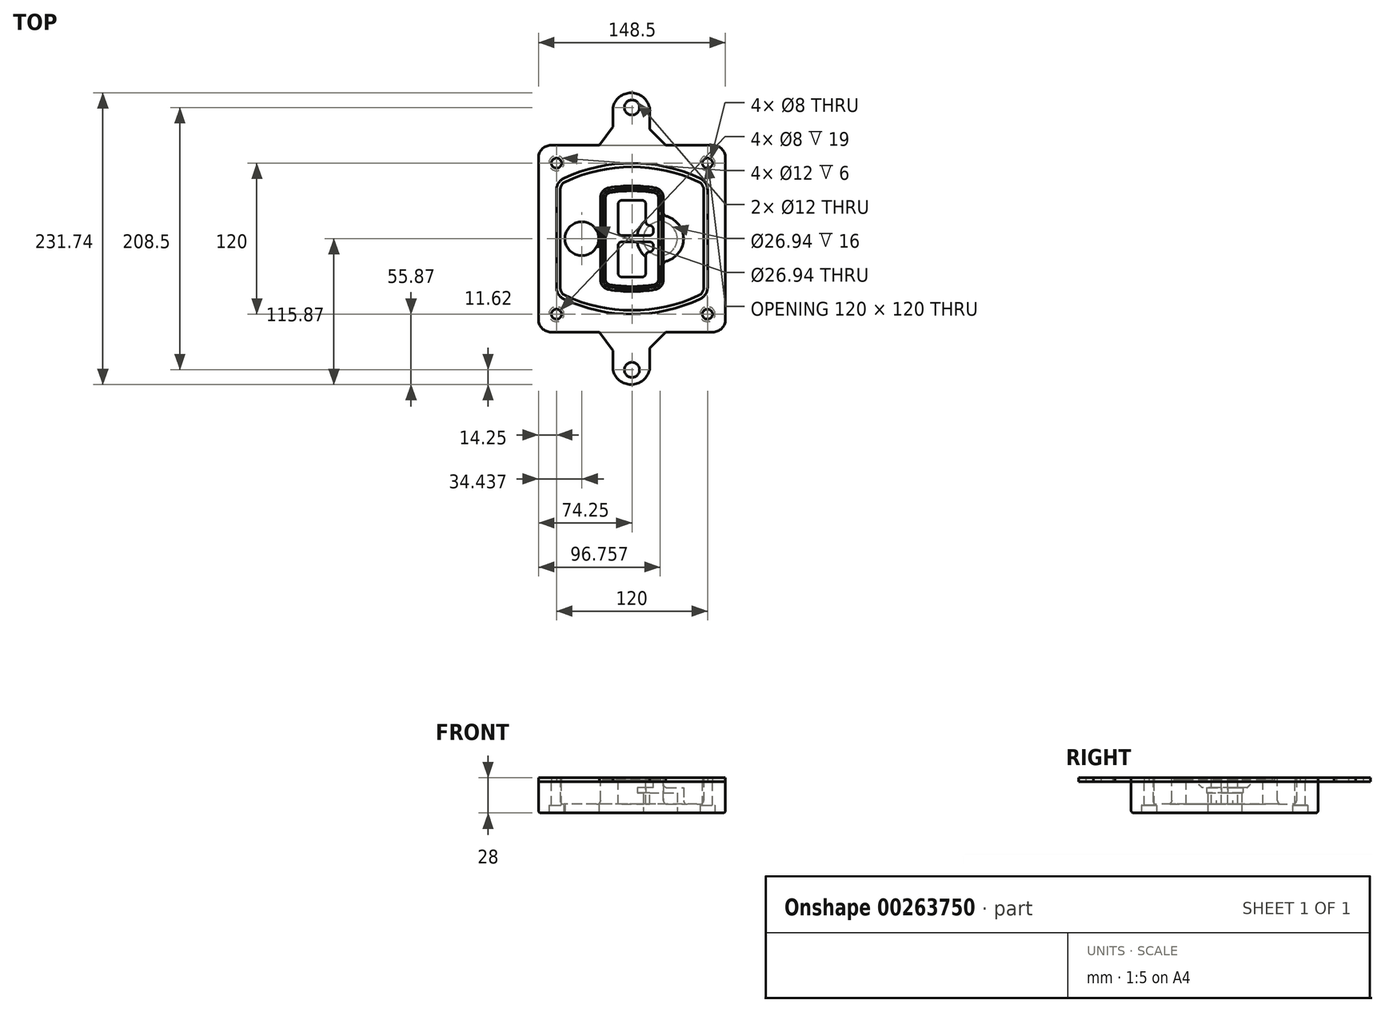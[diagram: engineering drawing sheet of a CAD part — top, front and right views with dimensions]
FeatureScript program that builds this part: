
annotation { "Feature Type Name" : "Feature", "Feature Type Description" : "" }
export const myFeature = defineFeature(function(context is Context, id is Id, definition is map)
    precondition{}
    {
        {
            var Q0;
            Q0=qCreatedBy(makeId("Top.planeOp"),FACE);
            var sketch = newSketch(context, id + "F0", { "sketchPlane" : qUnion([Q0])});
            skPoint(sketch, "E0.rect.middle", {"position": v(0, 0) * mm});
            skLineSegment(sketch, "E1.bottom", {"start": v(-64.25, -74.25) * mm, "end": v(64.25, -74.25) * mm});
            skLineSegment(sketch, "E1.top", {"start": v(-64.25, 74.25) * mm, "end": v(64.25, 74.25) * mm});
            skLineSegment(sketch, "E1.left", {"start": v(-74.25, -64.25) * mm, "end": v(-74.25, 64.25) * mm});
            skLineSegment(sketch, "E1.right", {"start": v(74.25, -64.25) * mm, "end": v(74.25, 64.25) * mm});
            skLineSegment(sketch, "E2", {"start": v(-74.25, 74.25) * mm, "end": v(74.25, -74.25) * mm, "construction": true});
            skLineSegment(sketch, "E3", {"start": v(74.25, 74.25) * mm, "end": v(-74.25, -74.25) * mm, "construction": true});
            skCircle(sketch, "E4", {"center": v(-60, 60) * mm, "radius": 4 * mm});
            skCircle(sketch, "E5", {"center": v(60, 60) * mm, "radius": 4 * mm});
            skCircle(sketch, "E6", {"center": v(60, -60) * mm, "radius": 4 * mm});
            skCircle(sketch, "E7", {"center": v(-60, -60) * mm, "radius": 4 * mm});
            skLineSegment(sketch, "E8", {"start": v(-60, 60) * mm, "end": v(60, 60) * mm, "construction": true});
            skLineSegment(sketch, "E9", {"start": v(60, 60) * mm, "end": v(60, -60) * mm, "construction": true});
            skLineSegment(sketch, "E10", {"start": v(60, -60) * mm, "end": v(-60, -60) * mm, "construction": true});
            skLineSegment(sketch, "E11", {"start": v(-60, -60) * mm, "end": v(-60, 60) * mm, "construction": true});
            skLineSegment(sketch, "E12", {"start": v(-60, 38.83) * mm, "end": v(-60, -38.83) * mm});
            skLineSegment(sketch, "E13", {"start": v(60, 38.83) * mm, "end": v(60, -38.83) * mm});
            skArc(sketch, "E14", {"start": v(54.26, 47.88) * mm, "mid": v(0, 60) * mm, "end": v(-54.26, 47.88) * mm});
            skArc(sketch, "E15", {"start": v(-54.26, -47.88) * mm, "mid": v(0, -60) * mm, "end": v(54.26, -47.88) * mm});
            skLineSegment(sketch, "E16", {"start": v(-60, 0) * mm, "end": v(60, 0) * mm, "construction": true});
            skPoint(sketch, "E17.visualSharp", {"position": v(-60, -45) * mm});
            skArc(sketch, "E17.filletArc", {"start": v(-60, -38.83) * mm, "mid": v(-58.44, -44.2) * mm, "end": v(-54.26, -47.88) * mm});
            skPoint(sketch, "E18.visualSharp", {"position": v(-60, 45) * mm});
            skArc(sketch, "E18.filletArc", {"start": v(-54.26, 47.88) * mm, "mid": v(-58.44, 44.2) * mm, "end": v(-60, 38.83) * mm});
            skPoint(sketch, "E19.visualSharp", {"position": v(60, 45) * mm});
            skArc(sketch, "E19.filletArc", {"start": v(60, 38.83) * mm, "mid": v(58.44, 44.2) * mm, "end": v(54.26, 47.88) * mm});
            skPoint(sketch, "E20.visualSharp", {"position": v(60, -45) * mm});
            skArc(sketch, "E20.filletArc", {"start": v(54.26, -47.88) * mm, "mid": v(58.44, -44.2) * mm, "end": v(60, -38.83) * mm});
            skPoint(sketch, "E21.visualSharp", {"position": v(-74.25, 74.25) * mm});
            skArc(sketch, "E21.filletArc", {"start": v(-64.25, 74.25) * mm, "mid": v(-71.32, 71.32) * mm, "end": v(-74.25, 64.25) * mm});
            skPoint(sketch, "E22.visualSharp", {"position": v(74.25, 74.25) * mm});
            skArc(sketch, "E22.filletArc", {"start": v(74.25, 64.25) * mm, "mid": v(71.32, 71.32) * mm, "end": v(64.25, 74.25) * mm});
            skPoint(sketch, "E23.visualSharp", {"position": v(74.25, -74.25) * mm});
            skArc(sketch, "E23.filletArc", {"start": v(64.25, -74.25) * mm, "mid": v(71.32, -71.32) * mm, "end": v(74.25, -64.25) * mm});
            skPoint(sketch, "E24.visualSharp", {"position": v(-74.25, -74.25) * mm});
            skArc(sketch, "E24.filletArc", {"start": v(-74.25, -64.25) * mm, "mid": v(-71.32, -71.32) * mm, "end": v(-64.25, -74.25) * mm});
            skArc(sketch, "E25.0", {"start": v(57, 38.83) * mm, "mid": v(55.9, 42.58) * mm, "end": v(52.98, 45.17) * mm});
            skLineSegment(sketch, "E25.1", {"start": v(57, 38.83) * mm, "end": v(57, -38.83) * mm});
            skArc(sketch, "E25.2", {"start": v(52.98, -45.17) * mm, "mid": v(55.9, -42.58) * mm, "end": v(57, -38.83) * mm});
            skArc(sketch, "E25.3", {"start": v(-52.98, -45.17) * mm, "mid": v(0, -57) * mm, "end": v(52.98, -45.17) * mm});
            skArc(sketch, "E25.4", {"start": v(-57, -38.83) * mm, "mid": v(-55.9, -42.58) * mm, "end": v(-52.98, -45.17) * mm});
            skArc(sketch, "E25.5", {"start": v(52.98, 45.17) * mm, "mid": v(0, 57) * mm, "end": v(-52.98, 45.17) * mm});
            skLineSegment(sketch, "E25.6", {"start": v(-57, 38.83) * mm, "end": v(-57, -38.83) * mm});
            skArc(sketch, "E25.7", {"start": v(-52.98, 45.17) * mm, "mid": v(-55.9, 42.58) * mm, "end": v(-57, 38.83) * mm});
            skArc(sketch, "E26.0", {"start": v(-55.96, 51.5) * mm, "mid": v(-61.82, 46.33) * mm, "end": v(-64, 38.83) * mm});
            skArc(sketch, "E26.1", {"start": v(55.96, 51.5) * mm, "mid": v(0, 64) * mm, "end": v(-55.96, 51.5) * mm});
            skArc(sketch, "E26.2", {"start": v(64, 38.83) * mm, "mid": v(61.82, 46.33) * mm, "end": v(55.96, 51.5) * mm});
            skLineSegment(sketch, "E26.3", {"start": v(64, 38.83) * mm, "end": v(64, -38.83) * mm});
            skArc(sketch, "E26.4", {"start": v(55.96, -51.5) * mm, "mid": v(61.82, -46.33) * mm, "end": v(64, -38.83) * mm});
            skLineSegment(sketch, "E26.5", {"start": v(-64, 38.83) * mm, "end": v(-64, -38.83) * mm});
            skArc(sketch, "E26.6", {"start": v(-55.96, -51.5) * mm, "mid": v(0, -64) * mm, "end": v(55.96, -51.5) * mm});
            skArc(sketch, "E26.7", {"start": v(-64, -38.83) * mm, "mid": v(-61.82, -46.33) * mm, "end": v(-55.96, -51.5) * mm});
            skSolve(sketch);
        }
        {
            var Q0;
            Q0=makeQuery(id+"F0.imprint","IMPRINT",FACE,{"disambiguationData":[TD([[makeQuery(id+"F0.imprint","IMPRINT",EDGE,{"derivedFrom":sQuery(id+"F0.wireOp",EDGE,"E1.bottom")}),1.0]])]});
            var Q1;
            Q1=makeQuery(id+"F0.imprint","IMPRINT",FACE,{"disambiguationData":[TD([[makeQuery(id+"F0.imprint","IMPRINT",EDGE,{"derivedFrom":sQuery(id+"F0.wireOp",EDGE,"E12")}),1.0]])]});
            var Q2;
            Q2=makeQuery(id+"F0.imprint","IMPRINT",FACE,{"disambiguationData":[TD([[makeQuery(id+"F0.imprint","IMPRINT",EDGE,{"derivedFrom":sQuery(id+"F0.wireOp",EDGE,"E25.0")}),1.0]])]});
            var Q3;
            Q3=makeQuery(id+"F0.imprint","IMPRINT",FACE,{"disambiguationData":[TD([[makeQuery(id+"F0.imprint","IMPRINT",EDGE,{"derivedFrom":sQuery(id+"F0.wireOp",EDGE,"E12")}),-1.0]])]});
            extrude(context, id + "F1", {"entities" : qUnion([Q0, Q1, Q2, Q3]), "oppositeDirection" : true, "depth" : 25 * mm});
        }
        {
            var Q0;
            Q0=makeQuery(id+"F0.imprint","IMPRINT",FACE,{"disambiguationData":[TD([[makeQuery(id+"F0.imprint","IMPRINT",EDGE,{"derivedFrom":sQuery(id+"F0.wireOp",EDGE,"E12")}),1.0]])]});
            extrude(context, id + "F2", {"entities" : qUnion([Q0]), "operationType" : NewBodyOperationType.ADD, "depth" : 3 * mm});
        }
        {
            var Q0;
            Q0=makeQuery(id+"F0.imprint","IMPRINT",FACE,{"disambiguationData":[TD([[makeQuery(id+"F0.imprint","IMPRINT",EDGE,{"derivedFrom":sQuery(id+"F0.wireOp",EDGE,"E25.0")}),1.0]])]});
            extrude(context, id + "F3", {"entities" : qUnion([Q0]), "operationType" : NewBodyOperationType.REMOVE, "oppositeDirection" : true, "depth" : 18 * mm});
        }
        {
            var Q0;
            Q0=makeQuery(id+"F2.opExtrude","CAP_FACE",FACE,{"disambiguationData":[OSD([sQuery(id+"F0.wireOp",EDGE,"E12"),sQuery(id+"F0.wireOp",EDGE,"E13"),sQuery(id+"F0.wireOp",EDGE,"E14"),sQuery(id+"F0.wireOp",EDGE,"E15"),sQuery(id+"F0.wireOp",EDGE,"E17.filletArc"),sQuery(id+"F0.wireOp",EDGE,"E18.filletArc"),sQuery(id+"F0.wireOp",EDGE,"E19.filletArc"),sQuery(id+"F0.wireOp",EDGE,"E20.filletArc"),sQuery(id+"F0.wireOp",EDGE,"E25.0"),sQuery(id+"F0.wireOp",EDGE,"E25.1"),sQuery(id+"F0.wireOp",EDGE,"E25.2"),sQuery(id+"F0.wireOp",EDGE,"E25.3"),sQuery(id+"F0.wireOp",EDGE,"E25.4"),sQuery(id+"F0.wireOp",EDGE,"E25.5"),sQuery(id+"F0.wireOp",EDGE,"E25.6"),sQuery(id+"F0.wireOp",EDGE,"E25.7")])],"isStart":false});
            var sketch = newSketch(context, id + "F4", { "sketchPlane" : qUnion([Q0])});
            skArc(sketch, "E27.0", {"start": v(-18.34, -40.45) * mm, "mid": v(0, -42) * mm, "end": v(18.34, -40.45) * mm});
            skArc(sketch, "E28.0", {"start": v(18.34, 40.45) * mm, "mid": v(0, 42) * mm, "end": v(-18.34, 40.45) * mm});
            skLineSegment(sketch, "E29", {"start": v(-25, 32.57) * mm, "end": v(-25, -32.57) * mm});
            skLineSegment(sketch, "E30", {"start": v(25, 32.57) * mm, "end": v(25, -32.57) * mm});
            skLineSegment(sketch, "E31", {"start": v(-25, 39.1) * mm, "end": v(25, 39.1) * mm, "construction": true});
            skLineSegment(sketch, "E32", {"start": v(-25, -39.1) * mm, "end": v(25, -39.1) * mm, "construction": true});
            skPoint(sketch, "E33.visualSharp", {"position": v(-25, 39.1) * mm});
            skArc(sketch, "E33.filletArc", {"start": v(-18.34, 40.45) * mm, "mid": v(-23.11, 37.73) * mm, "end": v(-25, 32.57) * mm});
            skPoint(sketch, "E34.visualSharp", {"position": v(25, 39.1) * mm});
            skArc(sketch, "E34.filletArc", {"start": v(25, 32.57) * mm, "mid": v(23.11, 37.73) * mm, "end": v(18.34, 40.45) * mm});
            skPoint(sketch, "E35.visualSharp", {"position": v(25, -39.1) * mm});
            skArc(sketch, "E35.filletArc", {"start": v(18.34, -40.45) * mm, "mid": v(23.11, -37.73) * mm, "end": v(25, -32.57) * mm});
            skPoint(sketch, "E36.visualSharp", {"position": v(-25, -39.1) * mm});
            skArc(sketch, "E36.filletArc", {"start": v(-25, -32.57) * mm, "mid": v(-23.11, -37.73) * mm, "end": v(-18.34, -40.45) * mm});
            skArc(sketch, "E37.0", {"start": v(52.98, 45.17) * mm, "mid": v(0, 57) * mm, "end": v(-52.98, 45.17) * mm});
            skArc(sketch, "E37.1", {"start": v(-52.98, 45.17) * mm, "mid": v(-55.9, 42.58) * mm, "end": v(-57, 38.83) * mm});
            skLineSegment(sketch, "E37.2", {"start": v(-57, 38.83) * mm, "end": v(-57, -38.83) * mm});
            skArc(sketch, "E37.3", {"start": v(-57, -38.83) * mm, "mid": v(-55.9, -42.58) * mm, "end": v(-52.98, -45.17) * mm});
            skArc(sketch, "E37.4", {"start": v(-52.98, -45.17) * mm, "mid": v(0, -57) * mm, "end": v(52.98, -45.17) * mm});
            skArc(sketch, "E37.5", {"start": v(52.98, -45.17) * mm, "mid": v(55.9, -42.58) * mm, "end": v(57, -38.83) * mm});
            skLineSegment(sketch, "E37.6", {"start": v(57, 38.83) * mm, "end": v(57, -38.83) * mm});
            skArc(sketch, "E37.7", {"start": v(57, 38.83) * mm, "mid": v(55.9, 42.58) * mm, "end": v(52.98, 45.17) * mm});
            skLineSegment(sketch, "E38.0", {"start": v(23, 32.57) * mm, "end": v(23, -32.57) * mm});
            skArc(sketch, "E38.1", {"start": v(18, -38.48) * mm, "mid": v(21.58, -36.44) * mm, "end": v(23, -32.57) * mm});
            skArc(sketch, "E38.2", {"start": v(-18, -38.48) * mm, "mid": v(0, -40) * mm, "end": v(18, -38.48) * mm});
            skArc(sketch, "E38.3", {"start": v(-23, -32.57) * mm, "mid": v(-21.58, -36.44) * mm, "end": v(-18, -38.48) * mm});
            skLineSegment(sketch, "E38.4", {"start": v(-23, 32.57) * mm, "end": v(-23, -32.57) * mm});
            skArc(sketch, "E38.5", {"start": v(23, 32.57) * mm, "mid": v(21.58, 36.44) * mm, "end": v(18, 38.48) * mm});
            skArc(sketch, "E38.6", {"start": v(-18, 38.48) * mm, "mid": v(-21.58, 36.44) * mm, "end": v(-23, 32.57) * mm});
            skArc(sketch, "E38.7", {"start": v(18, 38.48) * mm, "mid": v(0, 40) * mm, "end": v(-18, 38.48) * mm});
            skArc(sketch, "E39.0", {"start": v(21, 32.57) * mm, "mid": v(20.06, 35.15) * mm, "end": v(17.67, 36.5) * mm});
            skLineSegment(sketch, "E39.1", {"start": v(21, 32.57) * mm, "end": v(21, -32.57) * mm});
            skArc(sketch, "E39.2", {"start": v(17.67, -36.5) * mm, "mid": v(20.06, -35.15) * mm, "end": v(21, -32.57) * mm});
            skArc(sketch, "E39.3", {"start": v(-17.67, -36.5) * mm, "mid": v(0, -38) * mm, "end": v(17.67, -36.5) * mm});
            skArc(sketch, "E39.4", {"start": v(-21, -32.57) * mm, "mid": v(-20.06, -35.15) * mm, "end": v(-17.67, -36.5) * mm});
            skArc(sketch, "E39.5", {"start": v(17.67, 36.5) * mm, "mid": v(0, 38) * mm, "end": v(-17.67, 36.5) * mm});
            skLineSegment(sketch, "E39.6", {"start": v(-21, 32.57) * mm, "end": v(-21, -32.57) * mm});
            skArc(sketch, "E39.7", {"start": v(-17.67, 36.5) * mm, "mid": v(-20.06, 35.15) * mm, "end": v(-21, 32.57) * mm});
            skLineSegment(sketch, "E40", {"start": v(-25, 0) * mm, "end": v(25, 0) * mm, "construction": true});
            skLineSegment(sketch, "E41", {"start": v(-11, 5.5) * mm, "end": v(-11, 27.5) * mm});
            skLineSegment(sketch, "E42", {"start": v(-8, 30.5) * mm, "end": v(8, 30.5) * mm});
            skLineSegment(sketch, "E43", {"start": v(11, 27.5) * mm, "end": v(11, 13.5) * mm});
            skLineSegment(sketch, "E44", {"start": v(14, 10.5) * mm, "end": v(14, 10.5) * mm});
            skLineSegment(sketch, "E45", {"start": v(17, 7.5) * mm, "end": v(17, 5.5) * mm});
            skLineSegment(sketch, "E46", {"start": v(14, 2.5) * mm, "end": v(-8, 2.5) * mm});
            skPoint(sketch, "E47.visualSharp", {"position": v(-11, 30.5) * mm});
            skArc(sketch, "E47.filletArc", {"start": v(-8, 30.5) * mm, "mid": v(-10.12, 29.62) * mm, "end": v(-11, 27.5) * mm});
            skPoint(sketch, "E48.visualSharp", {"position": v(11, 30.5) * mm});
            skArc(sketch, "E48.filletArc", {"start": v(11, 27.5) * mm, "mid": v(10.12, 29.62) * mm, "end": v(8, 30.5) * mm});
            skPoint(sketch, "E49.visualSharp", {"position": v(11, 10.5) * mm});
            skArc(sketch, "E49.filletArc", {"start": v(11, 13.5) * mm, "mid": v(11.88, 11.38) * mm, "end": v(14, 10.5) * mm});
            skPoint(sketch, "E50.visualSharp", {"position": v(17, 10.5) * mm});
            skArc(sketch, "E50.filletArc", {"start": v(17, 7.5) * mm, "mid": v(16.12, 9.62) * mm, "end": v(14, 10.5) * mm});
            skPoint(sketch, "E51.visualSharp", {"position": v(17, 2.5) * mm});
            skArc(sketch, "E51.filletArc", {"start": v(14, 2.5) * mm, "mid": v(16.12, 3.38) * mm, "end": v(17, 5.5) * mm});
            skPoint(sketch, "E52.visualSharp", {"position": v(-11, 2.5) * mm});
            skArc(sketch, "E52.filletArc", {"start": v(-11, 5.5) * mm, "mid": v(-10.12, 3.38) * mm, "end": v(-8, 2.5) * mm});
            skLineSegment(sketch, "E53.0.MirrorCS", {"start": v(14, -2.5) * mm, "end": v(-8, -2.5) * mm});
            skArc(sketch, "E54.0.MirrorCS", {"start": v(-11, -5.5) * mm, "mid": v(-10.12, -3.38) * mm, "end": v(-8, -2.5) * mm});
            skLineSegment(sketch, "E55.0.MirrorCS", {"start": v(-11, -5.5) * mm, "end": v(-11, -27.5) * mm});
            skArc(sketch, "E56.0.MirrorCS", {"start": v(-8, -30.5) * mm, "mid": v(-10.12, -29.62) * mm, "end": v(-11, -27.5) * mm});
            skLineSegment(sketch, "E57.0.MirrorCS", {"start": v(-8, -30.5) * mm, "end": v(8, -30.5) * mm});
            skArc(sketch, "E58.0.MirrorCS", {"start": v(11, -27.5) * mm, "mid": v(10.12, -29.62) * mm, "end": v(8, -30.5) * mm});
            skLineSegment(sketch, "E59.0.MirrorCS", {"start": v(11, -27.5) * mm, "end": v(11, -13.5) * mm});
            skArc(sketch, "E60.0.MirrorCS", {"start": v(11, -13.5) * mm, "mid": v(11.88, -11.38) * mm, "end": v(14, -10.5) * mm});
            skArc(sketch, "E61.0.MirrorCS", {"start": v(17, -7.5) * mm, "mid": v(16.12, -9.62) * mm, "end": v(14, -10.5) * mm});
            skLineSegment(sketch, "E62.0.MirrorCS", {"start": v(17, -7.5) * mm, "end": v(17, -5.5) * mm});
            skArc(sketch, "E63.0.MirrorCS", {"start": v(14, -2.5) * mm, "mid": v(16.12, -3.38) * mm, "end": v(17, -5.5) * mm});
            skSolve(sketch);
        }
        {
            var Q0;
            Q0=makeQuery(id+"F4.imprint","IMPRINT",FACE,{"disambiguationData":[TD([[makeQuery(id+"F4.imprint","IMPRINT",EDGE,{"derivedFrom":sQuery(id+"F4.wireOp",EDGE,"E27.0")}),1.0]])]});
            var Q1;
            Q1=makeQuery(id+"F4.imprint","IMPRINT",FACE,{"disambiguationData":[TD([[makeQuery(id+"F4.imprint","IMPRINT",EDGE,{"derivedFrom":sQuery(id+"F4.wireOp",EDGE,"E38.0")}),-1.0]])]});
            var Q2;
            Q2=makeQuery(id+"F4.imprint","IMPRINT",FACE,{"disambiguationData":[TD([[makeQuery(id+"F4.imprint","IMPRINT",EDGE,{"derivedFrom":sQuery(id+"F4.wireOp",EDGE,"E39.0")}),1.0]])]});
            extrude(context, id + "F5", {"entities" : qUnion([Q0, Q1, Q2]), "operationType" : NewBodyOperationType.ADD, "endBound" : BoundingType.UP_TO_NEXT, "oppositeDirection" : true, "depth" : 25 * mm});
        }
        {
            var Q0;
            Q0=makeQuery(id+"F4.imprint","IMPRINT",FACE,{"disambiguationData":[TD([[makeQuery(id+"F4.imprint","IMPRINT",EDGE,{"derivedFrom":sQuery(id+"F4.wireOp",EDGE,"E38.0")}),-1.0]])]});
            extrude(context, id + "F6", {"entities" : qUnion([Q0]), "operationType" : NewBodyOperationType.REMOVE, "oppositeDirection" : true, "depth" : 2 * mm});
        }
        {
            var Q0;
            Q0=makeQuery(id+"F1.opExtrude","CAP_FACE",FACE,{"disambiguationData":[OSD([sQuery(id+"F0.wireOp",EDGE,"E1.bottom"),sQuery(id+"F0.wireOp",EDGE,"E1.top"),sQuery(id+"F0.wireOp",EDGE,"E1.left"),sQuery(id+"F0.wireOp",EDGE,"E1.right"),sQuery(id+"F0.wireOp",EDGE,"E4"),sQuery(id+"F0.wireOp",EDGE,"E5"),sQuery(id+"F0.wireOp",EDGE,"E6"),sQuery(id+"F0.wireOp",EDGE,"E7"),sQuery(id+"F0.wireOp",EDGE,"E21.filletArc"),sQuery(id+"F0.wireOp",EDGE,"E22.filletArc"),sQuery(id+"F0.wireOp",EDGE,"E23.filletArc"),sQuery(id+"F0.wireOp",EDGE,"E24.filletArc")])],"isStart":false});
            var sketch = newSketch(context, id + "F7", { "sketchPlane" : qUnion([Q0])});
            skCircle(sketch, "E64", {"center": v(22.5, 0) * mm, "radius": 13.47 * mm});
            skCircle(sketch, "E65", {"center": v(-39.81, 0) * mm, "radius": 13.47 * mm});
            skLineSegment(sketch, "E66", {"start": v(74.25, 0) * mm, "end": v(-74.25, 0) * mm});
            skCircle(sketch, "E67", {"center": v(22.5, 0) * mm, "radius": 18.47 * mm});
            skCircle(sketch, "E68", {"center": v(60, -60) * mm, "radius": 6 * mm});
            skCircle(sketch, "E69", {"center": v(-60, -60) * mm, "radius": 6 * mm});
            skCircle(sketch, "E70", {"center": v(-60, 60) * mm, "radius": 6 * mm});
            skCircle(sketch, "E71", {"center": v(60, 60) * mm, "radius": 6 * mm});
            skSolve(sketch);
        }
        {
            var Q0;
            {var subQ1=sQuery(id+"F7.wireOp",EDGE,"E66");var subQ4=sQuery(id+"F7.wireOp",EDGE,"E64");var subQ6=makeQuery(id+"F7.imprint","INTERSECT",VERTEX,{"disambiguationData":[OD(0.0)],"derivedFrom":[subQ4,subQ1]});Q0=makeQuery(id+"F7.imprint","IMPRINT",FACE,{"disambiguationData":[TD([[makeQuery(id+"F7.imprint","IMPRINT",EDGE,{"disambiguationData":[TD([[subQ6,-1.0]])],"derivedFrom":subQ4}),-1.0]])]});}
            var Q1;
            {var subQ0=sQuery(id+"F7.wireOp",EDGE,"E66");var subQ1=sQuery(id+"F7.wireOp",EDGE,"E64");var subQ3=makeQuery(id+"F7.imprint","INTERSECT",VERTEX,{"disambiguationData":[OD(0.0)],"derivedFrom":[subQ1,subQ0]});Q1=makeQuery(id+"F7.imprint","IMPRINT",FACE,{"disambiguationData":[TD([[makeQuery(id+"F7.imprint","IMPRINT",EDGE,{"disambiguationData":[TD([[subQ3,-1.0]])],"derivedFrom":subQ1}),1.0]])]});}
            var Q2;
            {var subQ0=sQuery(id+"F7.wireOp",EDGE,"E66");var subQ1=sQuery(id+"F7.wireOp",EDGE,"E64");var subQ3=makeQuery(id+"F7.imprint","INTERSECT",VERTEX,{"disambiguationData":[OD(0.0)],"derivedFrom":[subQ1,subQ0]});Q2=makeQuery(id+"F7.imprint","IMPRINT",FACE,{"disambiguationData":[TD([[makeQuery(id+"F7.imprint","IMPRINT",EDGE,{"disambiguationData":[TD([[subQ3,1.0]])],"derivedFrom":subQ1}),1.0]])]});}
            var Q3;
            {var subQ1=sQuery(id+"F7.wireOp",EDGE,"E66");var subQ4=sQuery(id+"F7.wireOp",EDGE,"E64");var subQ6=makeQuery(id+"F7.imprint","INTERSECT",VERTEX,{"disambiguationData":[OD(0.0)],"derivedFrom":[subQ4,subQ1]});Q3=makeQuery(id+"F7.imprint","IMPRINT",FACE,{"disambiguationData":[TD([[makeQuery(id+"F7.imprint","IMPRINT",EDGE,{"disambiguationData":[TD([[subQ6,1.0]])],"derivedFrom":subQ4}),-1.0]])]});}
            extrude(context, id + "F8", {"entities" : qUnion([Q0, Q1, Q2, Q3]), "operationType" : NewBodyOperationType.ADD, "oppositeDirection" : true, "depth" : 20 * mm});
        }
        {
            var Q0;
            {var subQ0=sQuery(id+"F7.wireOp",EDGE,"E66");var subQ1=sQuery(id+"F7.wireOp",EDGE,"E64");var subQ3=makeQuery(id+"F7.imprint","INTERSECT",VERTEX,{"disambiguationData":[OD(0.0)],"derivedFrom":[subQ1,subQ0]});Q0=makeQuery(id+"F7.imprint","IMPRINT",FACE,{"disambiguationData":[TD([[makeQuery(id+"F7.imprint","IMPRINT",EDGE,{"disambiguationData":[TD([[subQ3,-1.0]])],"derivedFrom":subQ1}),1.0]])]});}
            var Q1;
            {var subQ0=sQuery(id+"F7.wireOp",EDGE,"E66");var subQ1=sQuery(id+"F7.wireOp",EDGE,"E64");var subQ3=makeQuery(id+"F7.imprint","INTERSECT",VERTEX,{"disambiguationData":[OD(0.0)],"derivedFrom":[subQ1,subQ0]});Q1=makeQuery(id+"F7.imprint","IMPRINT",FACE,{"disambiguationData":[TD([[makeQuery(id+"F7.imprint","IMPRINT",EDGE,{"disambiguationData":[TD([[subQ3,1.0]])],"derivedFrom":subQ1}),1.0]])]});}
            extrude(context, id + "F9", {"entities" : qUnion([Q0, Q1]), "operationType" : NewBodyOperationType.REMOVE, "oppositeDirection" : true, "depth" : 16 * mm});
        }
        {
            var Q0;
            {var subQ0=sQuery(id+"F7.wireOp",EDGE,"E66");var subQ1=sQuery(id+"F7.wireOp",EDGE,"E65");var subQ3=makeQuery(id+"F7.imprint","INTERSECT",VERTEX,{"disambiguationData":[OD(0.0)],"derivedFrom":[subQ1,subQ0]});Q0=makeQuery(id+"F7.imprint","IMPRINT",FACE,{"disambiguationData":[TD([[makeQuery(id+"F7.imprint","IMPRINT",EDGE,{"disambiguationData":[TD([[subQ3,-1.0]])],"derivedFrom":subQ1}),1.0]])]});}
            var Q1;
            {var subQ0=sQuery(id+"F7.wireOp",EDGE,"E66");var subQ1=sQuery(id+"F7.wireOp",EDGE,"E65");var subQ3=makeQuery(id+"F7.imprint","INTERSECT",VERTEX,{"disambiguationData":[OD(0.0)],"derivedFrom":[subQ1,subQ0]});Q1=makeQuery(id+"F7.imprint","IMPRINT",FACE,{"disambiguationData":[TD([[makeQuery(id+"F7.imprint","IMPRINT",EDGE,{"disambiguationData":[TD([[subQ3,1.0]])],"derivedFrom":subQ1}),1.0]])]});}
            extrude(context, id + "F10", {"entities" : qUnion([Q0, Q1]), "operationType" : NewBodyOperationType.REMOVE, "oppositeDirection" : true, "depth" : 25 * mm});
        }
        {
            var Q0;
            Q0=makeQuery(id+"F7.imprint","IMPRINT",FACE,{"disambiguationData":[TD([[makeQuery(id+"F7.imprint","IMPRINT",EDGE,{"derivedFrom":sQuery(id+"F7.wireOp",EDGE,"E68")}),1.0]])]});
            var Q1;
            Q1=makeQuery(id+"F7.imprint","IMPRINT",FACE,{"disambiguationData":[TD([[makeQuery(id+"F7.imprint","IMPRINT",EDGE,{"derivedFrom":makeQuery(id+"F1.opExtrude","CAP_EDGE",EDGE,{"disambiguationData":[OSD([sQuery(id+"F0.wireOp",EDGE,"E5")])],"isStart":false})}),-1.0]])]});
            var Q2;
            Q2=makeQuery(id+"F7.imprint","IMPRINT",FACE,{"disambiguationData":[TD([[makeQuery(id+"F7.imprint","IMPRINT",EDGE,{"derivedFrom":sQuery(id+"F7.wireOp",EDGE,"E69")}),1.0]])]});
            var Q3;
            Q3=makeQuery(id+"F7.imprint","IMPRINT",FACE,{"disambiguationData":[TD([[makeQuery(id+"F7.imprint","IMPRINT",EDGE,{"derivedFrom":makeQuery(id+"F1.opExtrude","CAP_EDGE",EDGE,{"disambiguationData":[OSD([sQuery(id+"F0.wireOp",EDGE,"E4")])],"isStart":false})}),-1.0]])]});
            var Q4;
            Q4=makeQuery(id+"F7.imprint","IMPRINT",FACE,{"disambiguationData":[TD([[makeQuery(id+"F7.imprint","IMPRINT",EDGE,{"derivedFrom":sQuery(id+"F7.wireOp",EDGE,"E70")}),1.0]])]});
            var Q5;
            Q5=makeQuery(id+"F7.imprint","IMPRINT",FACE,{"disambiguationData":[TD([[makeQuery(id+"F7.imprint","IMPRINT",EDGE,{"derivedFrom":makeQuery(id+"F1.opExtrude","CAP_EDGE",EDGE,{"disambiguationData":[OSD([sQuery(id+"F0.wireOp",EDGE,"E7")])],"isStart":false})}),-1.0]])]});
            var Q6;
            Q6=makeQuery(id+"F7.imprint","IMPRINT",FACE,{"disambiguationData":[TD([[makeQuery(id+"F7.imprint","IMPRINT",EDGE,{"derivedFrom":sQuery(id+"F7.wireOp",EDGE,"E71")}),1.0]])]});
            var Q7;
            Q7=makeQuery(id+"F7.imprint","IMPRINT",FACE,{"disambiguationData":[TD([[makeQuery(id+"F7.imprint","IMPRINT",EDGE,{"derivedFrom":makeQuery(id+"F1.opExtrude","CAP_EDGE",EDGE,{"disambiguationData":[OSD([sQuery(id+"F0.wireOp",EDGE,"E6")])],"isStart":false})}),-1.0]])]});
            extrude(context, id + "F11", {"entities" : qUnion([Q0, Q1, Q2, Q3, Q4, Q5, Q6, Q7]), "operationType" : NewBodyOperationType.REMOVE, "oppositeDirection" : true, "depth" : 6 * mm});
        }
        {
            var Q0;
            Q0=makeQuery(id+"F9.boolean.opBoolean","COPY",FACE,{"derivedFrom":makeQuery(id+"F9.opExtrude","CAP_FACE",FACE,{"disambiguationData":[OSD([sQuery(id+"F7.wireOp",EDGE,"E64")])],"isStart":false})});
            var sketch = newSketch(context, id + "F12", { "sketchPlane" : qUnion([Q0])});
            skArc(sketch, "E72.0", {"start": v(11, 14.45) * mm, "mid": v(6.45, 9.13) * mm, "end": v(4.2, 2.5) * mm});
            skArc(sketch, "E72.1", {"start": v(4.2, -2.5) * mm, "mid": v(6.45, -9.13) * mm, "end": v(11, -14.45) * mm});
            skLineSegment(sketch, "E73", {"start": v(4.2, -2.5) * mm, "end": v(14, -2.5) * mm});
            skLineSegment(sketch, "E74.0", {"start": v(14, 2.5) * mm, "end": v(4.2, 2.5) * mm});
            skArc(sketch, "E74.1", {"start": v(14, 2.5) * mm, "mid": v(16.12, 3.38) * mm, "end": v(17, 5.5) * mm});
            skLineSegment(sketch, "E74.2", {"start": v(17, 7.5) * mm, "end": v(17, 5.5) * mm});
            skArc(sketch, "E74.3", {"start": v(17, 7.5) * mm, "mid": v(16.12, 9.62) * mm, "end": v(14, 10.5) * mm});
            skArc(sketch, "E74.4", {"start": v(11, 13.5) * mm, "mid": v(11.88, 11.38) * mm, "end": v(14, 10.5) * mm});
            skLineSegment(sketch, "E74.5", {"start": v(11, 14.45) * mm, "end": v(11, 13.5) * mm});
            skLineSegment(sketch, "E74.7", {"start": v(14, -2.5) * mm, "end": v(4.2, -2.5) * mm});
            skArc(sketch, "E74.8", {"start": v(14, -2.5) * mm, "mid": v(16.12, -3.38) * mm, "end": v(17, -5.5) * mm});
            skLineSegment(sketch, "E74.9", {"start": v(17, -7.5) * mm, "end": v(17, -5.5) * mm});
            skArc(sketch, "E74.10", {"start": v(17, -7.5) * mm, "mid": v(16.12, -9.62) * mm, "end": v(14, -10.5) * mm});
            skArc(sketch, "E74.11", {"start": v(11, -13.5) * mm, "mid": v(11.88, -11.38) * mm, "end": v(14, -10.5) * mm});
            skLineSegment(sketch, "E74.12", {"start": v(11, -14.45) * mm, "end": v(11, -13.5) * mm});
            skPoint(sketch, "E75.orphan", {"position": v(11, -27.5) * mm});
            skPoint(sketch, "E76.orphan", {"position": v(-8, -2.5) * mm});
            skPoint(sketch, "E77.orphan", {"position": v(-8, 2.5) * mm});
            skPoint(sketch, "E78.orphan", {"position": v(11, 27.5) * mm});
            skSolve(sketch);
        }
        {
            var Q0;
            {var subQ7=sQuery(id+"F12.wireOp",EDGE,"E72.0");var subQ14=sQuery(id+"F12.wireOp",EDGE,"E72.1");var subQ16=sQuery(id+"F12.wireOp",EDGE,"E74.1");var subQ18=sQuery(id+"F12.wireOp",EDGE,"E74.8");Q0=qUnion([makeQuery(id+"F12.imprint","IMPRINT",FACE,{"disambiguationData":[TD([[makeQuery(id+"F12.imprint","IMPRINT",EDGE,{"derivedFrom":subQ7}),1.0]])]}),makeQuery(id+"F12.imprint","IMPRINT",FACE,{"disambiguationData":[TD([[makeQuery(id+"F12.imprint","IMPRINT",EDGE,{"derivedFrom":subQ14}),1.0]])]}),makeQuery(id+"F12.imprint","IMPRINT",FACE,{"disambiguationData":[TD([[makeQuery(id+"F12.imprint","IMPRINT",EDGE,{"derivedFrom":subQ16}),1.0]])]}),makeQuery(id+"F12.imprint","IMPRINT",FACE,{"disambiguationData":[TD([[makeQuery(id+"F12.imprint","IMPRINT",EDGE,{"derivedFrom":subQ18}),-1.0]])]})]);}
            var Q1;
            Q1=makeQuery(id+"F5.boolean.opBoolean","SPLIT",FACE,{"disambiguationData":[TD([makeQuery(id+"F5.opExtrude","SWEPT_FACE",FACE,{"disambiguationData":[OSD([sQuery(id+"F4.wireOp",EDGE,"E41")])]})])],"derivedFrom":makeQuery(id+"F3.boolean.opBoolean","COPY",FACE,{"derivedFrom":makeQuery(id+"F3.opExtrude","CAP_FACE",FACE,{"disambiguationData":[OSD([sQuery(id+"F0.wireOp",EDGE,"E25.0"),sQuery(id+"F0.wireOp",EDGE,"E25.1"),sQuery(id+"F0.wireOp",EDGE,"E25.2"),sQuery(id+"F0.wireOp",EDGE,"E25.3"),sQuery(id+"F0.wireOp",EDGE,"E25.4"),sQuery(id+"F0.wireOp",EDGE,"E25.5"),sQuery(id+"F0.wireOp",EDGE,"E25.6"),sQuery(id+"F0.wireOp",EDGE,"E25.7")])],"isStart":false})})});
            extrude(context, id + "F13", {"entities" : qUnion([Q0]), "operationType" : NewBodyOperationType.REMOVE, "endBound" : BoundingType.UP_TO_SURFACE, "endBoundEntityFace" : qUnion([Q1]), "depth" : 25 * mm});
        }
        {
            var Q0;
            Q0=makeQuery(id+"F3.boolean.opBoolean","COPY",EDGE,{"derivedFrom":makeQuery(id+"F3.opExtrude","CAP_EDGE",EDGE,{"disambiguationData":[OSD([sQuery(id+"F0.wireOp",EDGE,"E25.6")])],"isStart":false})});
            var Q1;
            Q1=makeQuery(id+"F8.boolean.opBoolean","INTERSECT",EDGE,{"derivedFrom":[makeQuery(id+"F5.opExtrude","SWEPT_FACE",FACE,{"disambiguationData":[OSD([sQuery(id+"F4.wireOp",EDGE,"E30")])]}),makeQuery(id+"F8.opExtrude","CAP_FACE",FACE,{"disambiguationData":[OSD([sQuery(id+"F7.wireOp",EDGE,"E67")])],"isStart":false})]});
            var Q2;
            Q2=makeQuery(id+"F8.boolean.opBoolean","INTERSECT",EDGE,{"disambiguationData":[OD(1.0)],"derivedFrom":[makeQuery(id+"F5.opExtrude","SWEPT_FACE",FACE,{"disambiguationData":[OSD([sQuery(id+"F4.wireOp",EDGE,"E30")])]}),makeQuery(id+"F8.opExtrude","SWEPT_FACE",FACE,{"disambiguationData":[OSD([sQuery(id+"F7.wireOp",EDGE,"E67")])]})]});
            var Q3;
            {var subQ0=sQuery(id+"F4.wireOp",EDGE,"E30");Q3=makeQuery(id+"F8.boolean.opBoolean","SPLIT",EDGE,{"disambiguationData":[TD([makeQuery(id+"F5.opExtrude","SWEPT_FACE",FACE,{"disambiguationData":[OSD([sQuery(id+"F4.wireOp",EDGE,"E35.filletArc")])]})])],"derivedFrom":makeQuery(id+"F5.opExtrude","CAP_EDGE",EDGE,{"disambiguationData":[OSD([subQ0])],"isStart":false})});}
            var Q4;
            {var subQ0=sQuery(id+"F0.wireOp",EDGE,"E25.7");var subQ1=sQuery(id+"F0.wireOp",EDGE,"E25.1");var subQ2=sQuery(id+"F0.wireOp",EDGE,"E25.6");var subQ3=sQuery(id+"F0.wireOp",EDGE,"E25.5");var subQ4=sQuery(id+"F0.wireOp",EDGE,"E25.4");var subQ5=sQuery(id+"F0.wireOp",EDGE,"E25.0");var subQ6=sQuery(id+"F0.wireOp",EDGE,"E25.2");var subQ7=sQuery(id+"F0.wireOp",EDGE,"E25.3");Q4=makeQuery(id+"F8.boolean.opBoolean","INTERSECT",EDGE,{"derivedFrom":[makeQuery(id+"F5.boolean.opBoolean","SPLIT",FACE,{"disambiguationData":[TD([makeQuery(id+"F2.opExtrude","SWEPT_FACE",FACE,{"disambiguationData":[OSD([subQ5])]})])],"derivedFrom":makeQuery(id+"F3.boolean.opBoolean","COPY",FACE,{"derivedFrom":makeQuery(id+"F3.opExtrude","CAP_FACE",FACE,{"disambiguationData":[OSD([subQ5,subQ1,subQ6,subQ7,subQ4,subQ3,subQ2,subQ0])],"isStart":false})})}),makeQuery(id+"F8.opExtrude","SWEPT_FACE",FACE,{"disambiguationData":[OSD([sQuery(id+"F7.wireOp",EDGE,"E67")])]})]});}
            var Q5;
            Q5=makeQuery(id+"F8.boolean.opBoolean","INTERSECT",EDGE,{"disambiguationData":[OD(0.0)],"derivedFrom":[makeQuery(id+"F5.opExtrude","SWEPT_FACE",FACE,{"disambiguationData":[OSD([sQuery(id+"F4.wireOp",EDGE,"E30")])]}),makeQuery(id+"F8.opExtrude","SWEPT_FACE",FACE,{"disambiguationData":[OSD([sQuery(id+"F7.wireOp",EDGE,"E67")])]})]});
            fillet(context, id + "F14", {"entities" : qUnion([Q0, Q1, Q2, Q3, Q4, Q5]), "radius" : 3 * mm, "tangentPropagation" : true, "allowEdgeOverflow" : false});
        }
        {
            var Q0;
            Q0=makeQuery(id+"F1.opExtrude","CAP_EDGE",EDGE,{"disambiguationData":[OSD([sQuery(id+"F0.wireOp",EDGE,"E1.bottom")])],"isStart":false});
            fillet(context, id + "F15", {"entities" : qUnion([Q0]), "radius" : 2 * mm, "tangentPropagation" : true, "allowEdgeOverflow" : false});
        }
        {
            var Q0;
            {var subQ0=sQuery(id+"F0.wireOp",EDGE,"E22.filletArc");var subQ1=sQuery(id+"F0.wireOp",EDGE,"E7");var subQ2=sQuery(id+"F0.wireOp",EDGE,"E6");var subQ3=sQuery(id+"F0.wireOp",EDGE,"E5");var subQ4=sQuery(id+"F0.wireOp",EDGE,"E4");var subQ5=sQuery(id+"F0.wireOp",EDGE,"E1.bottom");var subQ6=sQuery(id+"F0.wireOp",EDGE,"E21.filletArc");var subQ7=sQuery(id+"F0.wireOp",EDGE,"E1.top");var subQ8=sQuery(id+"F0.wireOp",EDGE,"E1.left");var subQ9=sQuery(id+"F0.wireOp",EDGE,"E1.right");var subQ10=sQuery(id+"F0.wireOp",EDGE,"E23.filletArc");var subQ11=sQuery(id+"F0.wireOp",EDGE,"E24.filletArc");Q0=makeQuery(id+"F2.boolean.opBoolean","SPLIT",FACE,{"disambiguationData":[TD([makeQuery(id+"F1.opExtrude","SWEPT_FACE",FACE,{"disambiguationData":[OSD([subQ5])]})])],"derivedFrom":makeQuery(id+"F1.opExtrude","CAP_FACE",FACE,{"disambiguationData":[OSD([subQ5,subQ7,subQ8,subQ9,subQ4,subQ3,subQ2,subQ1,subQ6,subQ0,subQ10,subQ11])],"isStart":true})});}
            var sketch = newSketch(context, id + "F16", { "sketchPlane" : qUnion([Q0])});
            skLineSegment(sketch, "E79", {"start": v(0, 74.25) * mm, "end": v(0, 104.25) * mm});
            skCircle(sketch, "E80", {"center": v(0, 104.25) * mm, "radius": 6 * mm});
            skLineSegment(sketch, "E81", {"start": v(-25.74, 74.25) * mm, "end": v(-15.24, 88.87) * mm});
            skLineSegment(sketch, "E82", {"start": v(-15.24, 88.87) * mm, "end": v(-15.24, 104.27) * mm});
            skLineSegment(sketch, "E83", {"start": v(26.71, 74.25) * mm, "end": v(13.98, 86.98) * mm});
            skLineSegment(sketch, "E84", {"start": v(13.98, 86.98) * mm, "end": v(13.98, 104.25) * mm});
            skArc(sketch, "E85", {"start": v(13.98, 104.25) * mm, "mid": v(-0.62, 115.87) * mm, "end": v(-15.24, 104.27) * mm});
            skLineSegment(sketch, "E86", {"start": v(-74.25, 0) * mm, "end": v(74.25, 0) * mm, "construction": true});
            skLineSegment(sketch, "E87.MirrorCS", {"start": v(-15.24, -88.87) * mm, "end": v(-15.24, -104.27) * mm});
            skLineSegment(sketch, "E88.MirrorCS", {"start": v(-25.74, -74.25) * mm, "end": v(-15.24, -88.87) * mm});
            skLineSegment(sketch, "E89.MirrorCS", {"start": v(0, -74.25) * mm, "end": v(0, -104.25) * mm});
            skLineSegment(sketch, "E90.MirrorCS", {"start": v(26.71, -74.25) * mm, "end": v(13.98, -86.98) * mm});
            skLineSegment(sketch, "E91.MirrorCS", {"start": v(13.98, -86.98) * mm, "end": v(13.98, -104.25) * mm});
            skArc(sketch, "E92.MirrorCS", {"start": v(13.98, -104.25) * mm, "mid": v(-0.62, -115.87) * mm, "end": v(-15.24, -104.27) * mm});
            skCircle(sketch, "E93.MirrorC", {"center": v(0, -104.25) * mm, "radius": 6 * mm});
            skSolve(sketch);
        }
        {
            var Q0;
            Q0=makeQuery(id+"F16.imprint","IMPRINT",FACE,{"disambiguationData":[TD([[makeQuery(id+"F16.imprint","IMPRINT",EDGE,{"derivedFrom":sQuery(id+"F16.wireOp",EDGE,"E80")}),-1.0]])]});
            var Q1;
            Q1=makeQuery(id+"F16.imprint","IMPRINT",FACE,{"disambiguationData":[TD([[makeQuery(id+"F16.imprint","IMPRINT",EDGE,{"derivedFrom":makeQuery(id+"F1.opExtrude","CAP_EDGE",EDGE,{"disambiguationData":[OSD([sQuery(id+"F0.wireOp",EDGE,"E1.left")])],"isStart":true})}),-1.0]])]});
            var Q2;
            Q2=makeQuery(id+"F16.imprint","IMPRINT",FACE,{"disambiguationData":[TD([[makeQuery(id+"F16.imprint","IMPRINT",EDGE,{"derivedFrom":sQuery(id+"F16.wireOp",EDGE,"E87.MirrorCS")}),1.0]])]});
            extrude(context, id + "F17", {"entities" : qUnion([Q0, Q1, Q2]), "depth" : 3 * mm});
        }
    });
